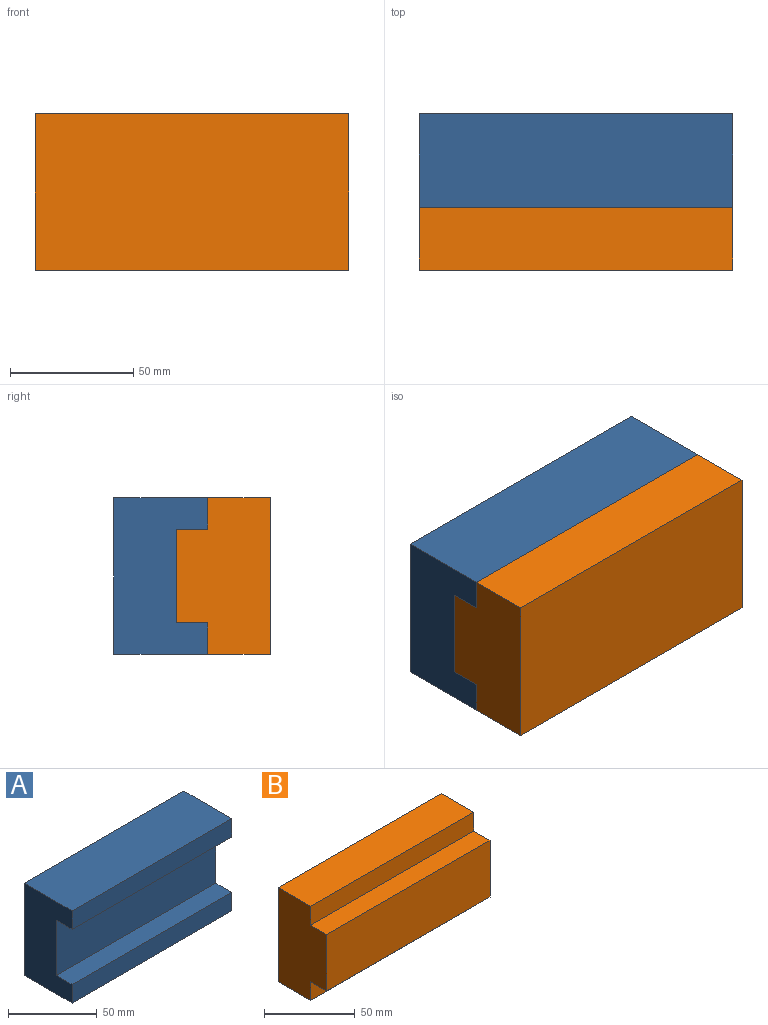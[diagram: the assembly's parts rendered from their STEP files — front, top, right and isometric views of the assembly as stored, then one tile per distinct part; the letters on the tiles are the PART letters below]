
ASSEMBLY  parts=2 mates=1
PART A: 10 faces, bbox 127x38.1x63.5 mm
  f0: plane 127x12.7mm, normal (0,-1,0), area 1612.9mm2, adj f1,f2,f3,f7
  f1: plane 63.5x38.1mm, normal (-1,0,0), area 1935.5mm2, adj f0,f3,f4,f5,f6,f7,f8,f9
  f2: plane 63.5x38.1mm, normal (1,0,0), area 1935.5mm2, adj f0,f3,f4,f5,f6,f7,f8,f9
  f3: plane 127x38.1mm, normal (0,0,1), area 4838.7mm2, adj f0,f1,f2,f6
  f4: plane 127x38.1mm, normal (0,0,-1), area 4838.7mm2, adj f1,f2,f5,f6
  f5: plane 127x12.7mm, normal (0,-1,0), area 1612.9mm2, adj f1,f2,f4,f8
  f6: plane 127x63.5mm, normal (0,1,0), area 8064.5mm2, adj f1,f2,f3,f4
  f7: plane 127x12.7mm, normal (0,0,-1), area 1612.9mm2, adj f0,f1,f2,f9
  f8: plane 127x12.7mm, normal (0,0,1), area 1612.9mm2, adj f1,f2,f5,f9
  f9: plane 127x38.1mm, normal (0,-1,0), area 4838.7mm2, adj f1,f2,f7,f8
PART B: 10 faces, bbox 127x38.1x63.5 mm
  f0: plane 63.5x38.1mm, normal (-1,0,0), area 2096.8mm2, adj f1,f3,f4,f5,f6,f7,f8,f9
  f1: plane 127x25.4mm, normal (0,0,-1), area 3225.8mm2, adj f0,f2,f5,f9
  f2: plane 63.5x38.1mm, normal (1,0,0), area 2096.8mm2, adj f1,f3,f4,f5,f6,f7,f8,f9
  f3: plane 127x38.1mm, normal (0,-1,0), area 4838.7mm2, adj f0,f2,f6,f8
  f4: plane 127x25.4mm, normal (0,0,1), area 3225.8mm2, adj f0,f2,f5,f7
  f5: plane 127x63.5mm, normal (0,1,0), area 8064.5mm2, adj f0,f1,f2,f4
  f6: plane 127x12.7mm, normal (0,0,1), area 1612.9mm2, adj f0,f2,f3,f7
  f7: plane 127x12.7mm, normal (0,-1,0), area 1612.9mm2, adj f0,f2,f4,f6
  f8: plane 127x12.7mm, normal (0,0,-1), area 1612.9mm2, adj f0,f2,f3,f9
  f9: plane 127x12.7mm, normal (0,-1,0), area 1612.9mm2, adj f0,f1,f2,f8
PLACE A rot(axis=(0,-1,0),180deg) t=(-109.57,-28.25,9.05)mm
PLACE B rot(axis=(0,0,1),180deg) t=(-109.57,-91.75,9.05)mm
MATE slider B.f0 <-> A.f1  axis (1,0,0) through (-46.07,-53.65,9.05)mm
